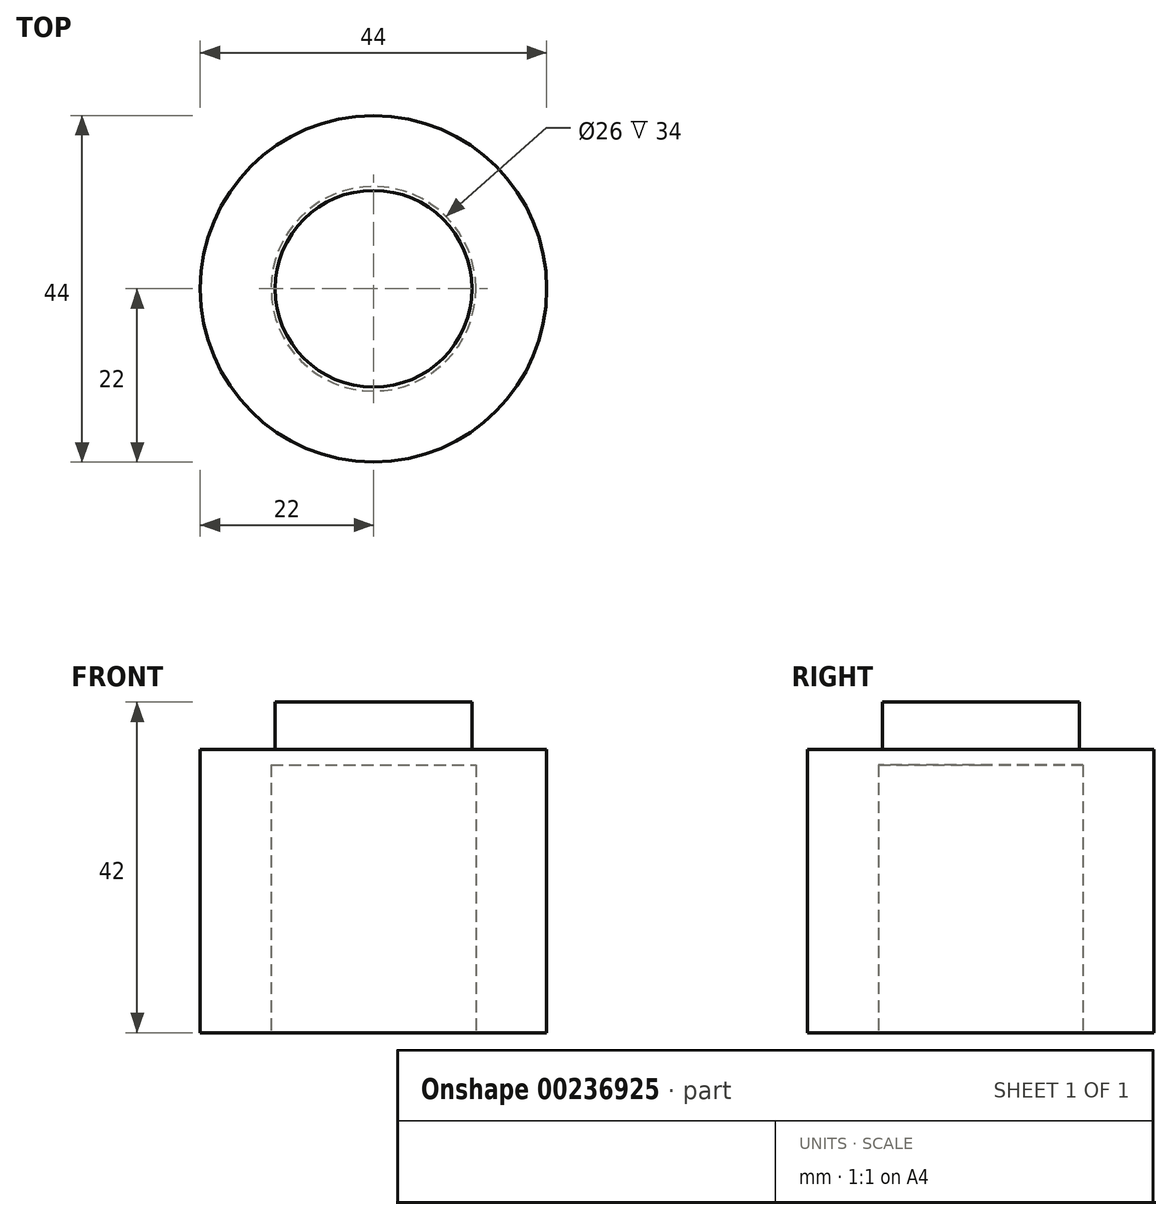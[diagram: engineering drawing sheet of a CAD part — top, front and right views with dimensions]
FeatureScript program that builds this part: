
annotation { "Feature Type Name" : "Feature", "Feature Type Description" : "" }
export const myFeature = defineFeature(function(context is Context, id is Id, definition is map)
    precondition{}
    {
        {
            var Q0;
            Q0=qCreatedBy(makeId("Top.planeOp"),FACE);
            var sketch = newSketch(context, id + "F0", { "sketchPlane" : qUnion([Q0])});
            skCircle(sketch, "E0", {"center": v(0, 0) * mm, "radius": 12.5 * mm});
            skSolve(sketch);
        }
        {
            var Q0;
            Q0 = qSketchRegion(id + "F0", true);
            extrude(context, id + "F1", {"entities" : qUnion([Q0]), "depth" : 6 * mm});
        }
        {
            var Q0;
            Q0=makeQuery(id+"F1.opExtrude","CAP_FACE",FACE,{"disambiguationData":[OSD([sQuery(id+"F0.wireOp",EDGE,"E0")])],"isStart":true});
            var sketch = newSketch(context, id + "F2", { "sketchPlane" : qUnion([Q0])});
            skCircle(sketch, "E1", {"center": v(0, 0) * mm, "radius": 22 * mm});
            skSolve(sketch);
        }
        {
            var Q0;
            Q0 = qSketchRegion(id + "F2", true);
            extrude(context, id + "F3", {"entities" : qUnion([Q0]), "operationType" : NewBodyOperationType.ADD, "depth" : 36 * mm});
        }
        {
            var Q0;
            Q0=makeQuery(id+"F3.opExtrude","CAP_FACE",FACE,{"disambiguationData":[OSD([sQuery(id+"F2.wireOp",EDGE,"E1")])],"isStart":false});
            var sketch = newSketch(context, id + "F4", { "sketchPlane" : qUnion([Q0])});
            skCircle(sketch, "E2", {"center": v(0, 0) * mm, "radius": 13 * mm});
            skSolve(sketch);
        }
        {
            var Q0;
            Q0 = qSketchRegion(id + "F4", true);
            extrude(context, id + "F5", {"entities" : qUnion([Q0]), "operationType" : NewBodyOperationType.REMOVE, "oppositeDirection" : true, "depth" : 34 * mm});
        }
    });
